# Revit family: P350200-031
name_source: partatom
category: Lighting Fixtures
units: mm (PartAtom-declared; Revit-internal decimal feet)

## family parameters
Cut with Voids When Loaded = No
Host = Face
Light Source = No
OmniClass Number = 23.80.70.11.14.17
OmniClass Title = Direct/Indirect
Part Type = Normal
Room Calculation Point = No
Round Connector Dimension = Use Diameter
Shared = Yes

## types (1)
- P350200-031
    Apparent Load = 60 VA
    Assembly Code = D5020200
    Clear Glass = Hubbell Glass
    Connector Description = Lighting Connector
    Default Elevation = 48 "
    Description = Perimeter Collection Two-Light Matte Black Modern Style Flush Mount Ceiling Light
    Features = Application: Inspired by geometric simplicity, the Perimeter Collection 2-Light Matte Black Modern Flush Mount Ceiling Light is ideal for any hallway, porch, stairwell, entryway, kitchen, or sitting room.
Styles: Perfect for contemporary, modern, and traditional style settings.
Finish: The square frame composed of clean, straight lines is coated in a classic matte black finish.
Materials: Constructed from steel to ensure a long product lifespan.
Glass/Shade: Light sources peek from inside the crisp open-frame design that accentuates the light fixture's modern aesthetic.
Bulbs: For ideal illumination, use 2 medium base bulbs that are sold separately (60w max - LED/CFL/incandescent). Compatible with dimmable bulbs.
Dimensions: Measures 12-inch width by 4-1/2-inch height.
Certifications: cCSAus damp location listed.
Pairs With: Pairs with the Glayse, Rae, and Elevate collections from Progress Lighting.
Warranty: Our 1-Year Limited Warranty guarantees your complete satisfaction with your purchase and includes professional after-sales customer service support.
    Fixture distribution = Direct
    Glass = Paint - Hubbell - White Texture
    Gold = Hubbell - Gold
    Housing Material = Paint - Hubbell - Textured Camera Black
    Lamp = LED/CFL/incandescent
    Load Classification = Lighting
    Manufacturer = Progress Lighting
    Model = P350200-031
    Power Factor = 1
    Product Documentation Link = https://hubbellcdn.com
    Product Link = https://www.hubbell.com
    URL = https://www.hubbell.com
    Voltage = 120 V
    Warranty = 1 year Warranty
    Wattage Comments = 60W
    Watts = 60 W
    Widh = 12 "

## geometry (parser evidence)
native form markers: Sweep x5
no freeform markers — native parametric forms only
